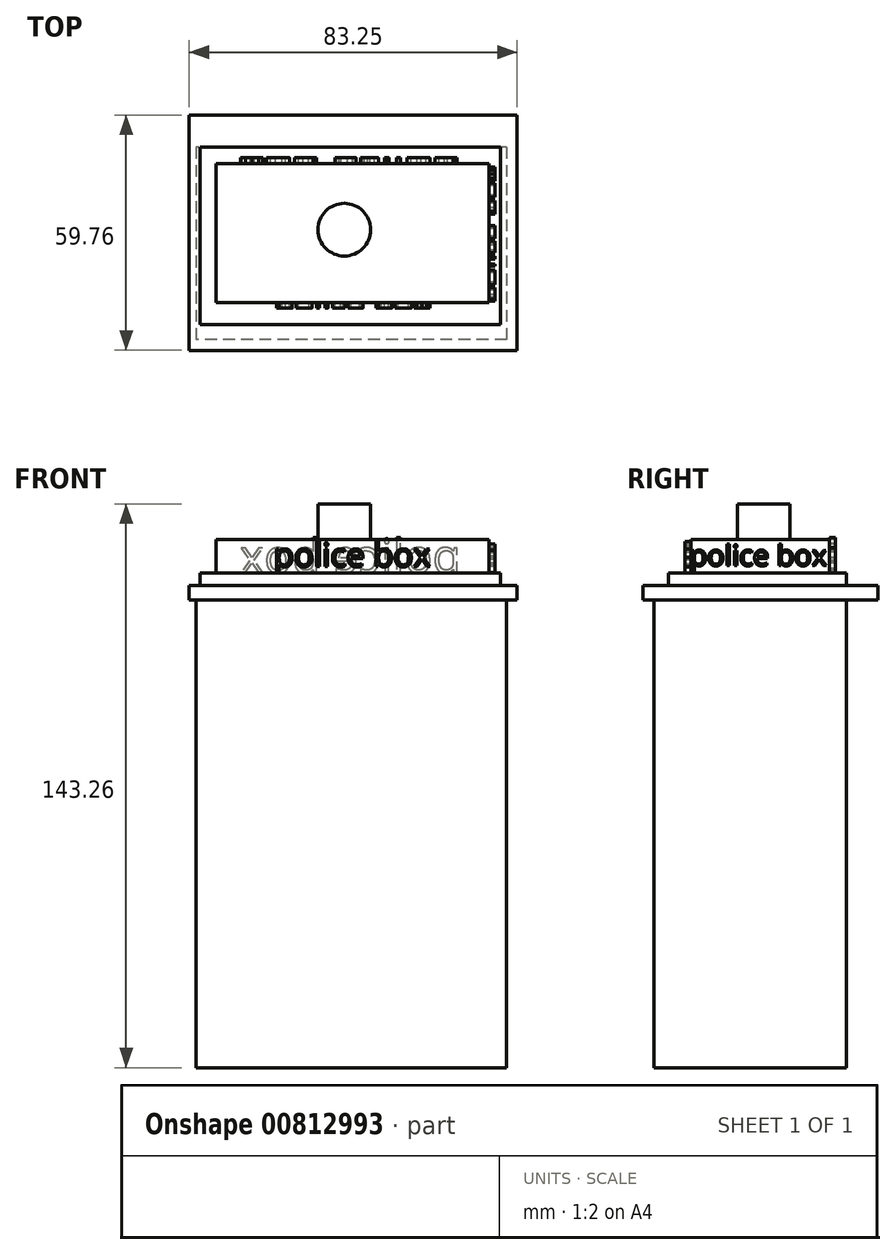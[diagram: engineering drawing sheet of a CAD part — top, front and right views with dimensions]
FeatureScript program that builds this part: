
annotation { "Feature Type Name" : "Feature", "Feature Type Description" : "" }
export const myFeature = defineFeature(function(context is Context, id is Id, definition is map)
    precondition{}
    {
        {
            var Q0;
            Q0=qCreatedBy(makeId("Front.planeOp"),FACE);
            var sketch = newSketch(context, id + "F0", { "sketchPlane" : qUnion([Q0])});
            skLineSegment(sketch, "E0.bottom", {"start": v(-33, 57.48) * mm, "end": v(45.85, 57.48) * mm});
            skLineSegment(sketch, "E0.top", {"start": v(-33, -62.96) * mm, "end": v(45.85, -62.96) * mm});
            skLineSegment(sketch, "E0.left", {"start": v(-33, 57.48) * mm, "end": v(-33, -62.96) * mm});
            skLineSegment(sketch, "E0.right", {"start": v(45.85, 57.48) * mm, "end": v(45.85, -62.96) * mm});
            skSolve(sketch);
        }
        {
            var Q0;
            Q0 = qSketchRegion(id + "F0", true);
            extrude(context, id + "F1", {"entities" : qUnion([Q0]), "depth" : 48.9 * mm, "offsetDistance" : 25 * mm});
        }
        {
            var Q0;
            Q0=qCreatedBy(makeId("Top.planeOp"),FACE);
            cPlane(context, id + "F2", {"entities" : qUnion([Q0]), "cplaneType" : CPlaneType.OFFSET, "offset" : 55.9 * mm, "width" : 150 * mm, "height" : 150 * mm});
        }
        {
            var Q0;
            Q0=qCreatedBy(id+"F2.planeOp",FACE);
            var sketch = newSketch(context, id + "F3", { "sketchPlane" : qUnion([Q0])});
            skLineSegment(sketch, "E1.bottom", {"start": v(-34.75, 8.09) * mm, "end": v(48.5, 8.09) * mm});
            skLineSegment(sketch, "E1.top", {"start": v(-34.75, -51.67) * mm, "end": v(48.5, -51.67) * mm});
            skLineSegment(sketch, "E1.left", {"start": v(-34.75, 8.09) * mm, "end": v(-34.75, -51.67) * mm});
            skLineSegment(sketch, "E1.right", {"start": v(48.5, 8.09) * mm, "end": v(48.5, -51.67) * mm});
            skSolve(sketch);
        }
        {
            var Q0;
            Q0 = qSketchRegion(id + "F3", true);
            extrude(context, id + "F4", {"entities" : qUnion([Q0]), "operationType" : NewBodyOperationType.ADD, "depth" : 3.7 * mm, "offsetDistance" : 25 * mm});
        }
        {
            var Q0;
            Q0=makeQuery(id+"F4.opExtrude","CAP_FACE",FACE,{"disambiguationData":[OSD([sQuery(id+"F3.wireOp",EDGE,"E1.bottom"),sQuery(id+"F3.wireOp",EDGE,"E1.top"),sQuery(id+"F3.wireOp",EDGE,"E1.left"),sQuery(id+"F3.wireOp",EDGE,"E1.right")])],"isStart":false});
            var sketch = newSketch(context, id + "F5", { "sketchPlane" : qUnion([Q0])});
            skLineSegment(sketch, "E2.bottom", {"start": v(-31.98, 0) * mm, "end": v(44.32, 0) * mm});
            skLineSegment(sketch, "E2.top", {"start": v(-31.98, -45.15) * mm, "end": v(44.32, -45.15) * mm});
            skLineSegment(sketch, "E2.left", {"start": v(-31.98, 0) * mm, "end": v(-31.98, -45.15) * mm});
            skLineSegment(sketch, "E2.right", {"start": v(44.32, 0) * mm, "end": v(44.32, -45.15) * mm});
            skSolve(sketch);
        }
        {
            var Q0;
            Q0 = qSketchRegion(id + "F5", true);
            extrude(context, id + "F6", {"entities" : qUnion([Q0]), "operationType" : NewBodyOperationType.ADD, "depth" : 3.1 * mm, "offsetDistance" : 25 * mm});
        }
        {
            var Q0;
            Q0=makeQuery(id+"F6.opExtrude","CAP_FACE",FACE,{"disambiguationData":[OSD([sQuery(id+"F5.wireOp",EDGE,"E2.bottom"),sQuery(id+"F5.wireOp",EDGE,"E2.top"),sQuery(id+"F5.wireOp",EDGE,"E2.left"),sQuery(id+"F5.wireOp",EDGE,"E2.right")])],"isStart":false});
            var sketch = newSketch(context, id + "F7", { "sketchPlane" : qUnion([Q0])});
            skLineSegment(sketch, "E3.bottom", {"start": v(-27.95, -4.24) * mm, "end": v(41.39, -4.24) * mm});
            skLineSegment(sketch, "E3.top", {"start": v(-27.95, -39.5) * mm, "end": v(41.39, -39.5) * mm});
            skLineSegment(sketch, "E3.left", {"start": v(-27.95, -4.24) * mm, "end": v(-27.95, -39.5) * mm});
            skLineSegment(sketch, "E3.right", {"start": v(41.39, -4.24) * mm, "end": v(41.39, -39.5) * mm});
            skSolve(sketch);
        }
        {
            var Q0;
            Q0 = qSketchRegion(id + "F7", true);
            extrude(context, id + "F8", {"entities" : qUnion([Q0]), "operationType" : NewBodyOperationType.ADD, "depth" : 8.5 * mm, "offsetDistance" : 25 * mm});
        }
        {
            var Q0;
            Q0=makeQuery(id+"F8.opExtrude","SWEPT_FACE",FACE,{"disambiguationData":[OSD([sQuery(id+"F7.wireOp",EDGE,"E3.top")])]});
            var sketch = newSketch(context, id + "F9", { "sketchPlane" : qUnion([Q0])});
            skPoint(sketch, "E4.firstSnap0", {"position": v(-27.95, 66.95) * mm});
            skText(sketch, "E5", { "text": "police box", "fontName": "OpenSans-Regular.ttf"});
            const initialGuessF9  = {"E5": [-0.01328, 0.06432, 1, 0, 0.00602]};
            skSetInitialGuess(sketch, initialGuessF9);
            skSolve(sketch);
        }
        {
            var Q0;
            Q0 = qSketchRegion(id + "F9", true);
            extrude(context, id + "F10", {"entities" : qUnion([Q0]), "operationType" : NewBodyOperationType.ADD, "depth" : 0.6 * mm, "offsetDistance" : 25 * mm});
        }
        {
            var Q0;
            Q0=makeQuery(id+"F8.opExtrude","CAP_FACE",FACE,{"disambiguationData":[OSD([sQuery(id+"F7.wireOp",EDGE,"E3.bottom"),sQuery(id+"F7.wireOp",EDGE,"E3.top"),sQuery(id+"F7.wireOp",EDGE,"E3.left"),sQuery(id+"F7.wireOp",EDGE,"E3.right")])],"isStart":false});
            var sketch = newSketch(context, id + "F11", { "sketchPlane" : qUnion([Q0])});
            skCircle(sketch, "E6", {"center": v(4.65, -21.02) * mm, "radius": 6.7 * mm});
            skSolve(sketch);
        }
        {
            var Q0;
            Q0 = qSketchRegion(id + "F11", true);
            extrude(context, id + "F12", {"entities" : qUnion([Q0]), "operationType" : NewBodyOperationType.ADD, "depth" : 9.1 * mm, "offsetDistance" : 25 * mm});
        }
        {
            var Q0;
            Q0 = qSketchRegion(id + "F9", true);
            extrude(context, id + "F13", {"entities" : qUnion([Q0]), "operationType" : NewBodyOperationType.ADD, "depth" : 1.5 * mm, "offsetDistance" : 25 * mm});
        }
        {
            var Q0;
            Q0=makeQuery(id+"F8.opExtrude","SWEPT_FACE",FACE,{"disambiguationData":[OSD([sQuery(id+"F7.wireOp",EDGE,"E3.right")])]});
            var sketch = newSketch(context, id + "F14", { "sketchPlane" : qUnion([Q0])});
            skText(sketch, "E7", { "text": "police box", "fontName": "OpenSans-Regular.ttf"});
            const initialGuessF14  = {"E7": [-0.03985, 0.06457, 1, 0, 0.00528]};
            skSetInitialGuess(sketch, initialGuessF14);
            skSolve(sketch);
        }
        {
            var Q0;
            Q0 = qSketchRegion(id + "F14", true);
            extrude(context, id + "F15", {"entities" : qUnion([Q0]), "operationType" : NewBodyOperationType.ADD, "depth" : 1.5 * mm, "offsetDistance" : 25 * mm});
        }
        {
            var Q0;
            Q0=makeQuery(id+"F8.opExtrude","SWEPT_FACE",FACE,{"disambiguationData":[OSD([sQuery(id+"F7.wireOp",EDGE,"E3.bottom")])]});
            var sketch = newSketch(context, id + "F16", { "sketchPlane" : qUnion([Q0])});
            skText(sketch, "E8", { "text": "police box\n", "fontName": "OpenSans-Regular.ttf"});
            const initialGuessF16  = {"E8": [-0.03428, 0.0628, 1, -0.00165, 0.0085]};
            skSetInitialGuess(sketch, initialGuessF16);
            skSolve(sketch);
        }
        {
            var Q0;
            Q0 = qSketchRegion(id + "F16", true);
            extrude(context, id + "F17", {"entities" : qUnion([Q0]), "operationType" : NewBodyOperationType.ADD, "depth" : 1.5 * mm, "offsetDistance" : 25 * mm});
        }
    });
